# Revit family: 24913 - Deca_Chuveiro Quadrado de Teto_1934.TET
name_source: partatom
category: Plumbing Fixtures
units: mm (PartAtom-declared; Revit-internal decimal feet)

## family parameters
Cut with Voids When Loaded = No
Host = Face
Part Type = Normal
Room Calculation Point = No
Round Connector Dimension = Use Radius
Shared = No

## types (3) — shared parameters
Acompanha o Produto = -
Aprovado por = quattroD
Atendimento ao Cliente = 0800 011 7073
Categoria = CHUVEIROS E DUCHAS
Composição Anel Vedação = -
Composição Assento = -
Composição Básica = Liga cobre (bronze e latão),Aço,Plástico de Engenharia,Elastômeros
Composição Componente = -
Consumo = -
Cor Interna = -
Cor Secundária = -
Cores Componente = -
Criado por = quattroD
Código Pai = 1934.C.TET
Diâmetro Água Fria = 0.02 m
Informações Complementares = -
Itens de Instalação = -
Linha = Chuveiro Quadrado
Manufacturer = Deca
Norma = NBR 15206
Peso Líquido (Kg) = 1.308
Pressão máx. funcionamento = 40 mca
Pressão mín. Aquec. Acúmulo = 2 mca
Pressão mín. Aquec. Passagem = 2 mca
Pressão mín. funcionamento = 2 mca
Raio Água Fria = 0.01 m
Saída de Esgoto = -
Segmento = -
Tipo de dispositivo economizador = -
Tipo de mecanismo utilizado = -
Tipo de rosca de entrada = -
Tipo de rosca de saída = -
URL = www.deca.com.br
zero-valued in all types: CWFU, Default Elevation, HWFU, WFU

## per-type parameters (varying)
| type | Cor Principal | Description | Material | Model |
| 1934.C.TET_Cromado | Cromado | Chuveiro Quadrado de Teto Cromado | Deca_Cromado | 1934.C.TET |
| 1934.BL.TET.MT_Black Matte | Black Matte | Chuveiro Quadrado de Teto Black Matte | Deca_Black Matte | 1934.BL.TET.MT |
| 1934.SM.TET.MT_Summer Gold | Summer Gold | Chuveiro Quadrado de Teto Summer Gold | Deca_Summer Gold | 1934.SM.TET.MT |

## geometry (parser evidence)
native form markers: Sweep x1
no freeform markers — native parametric forms only
